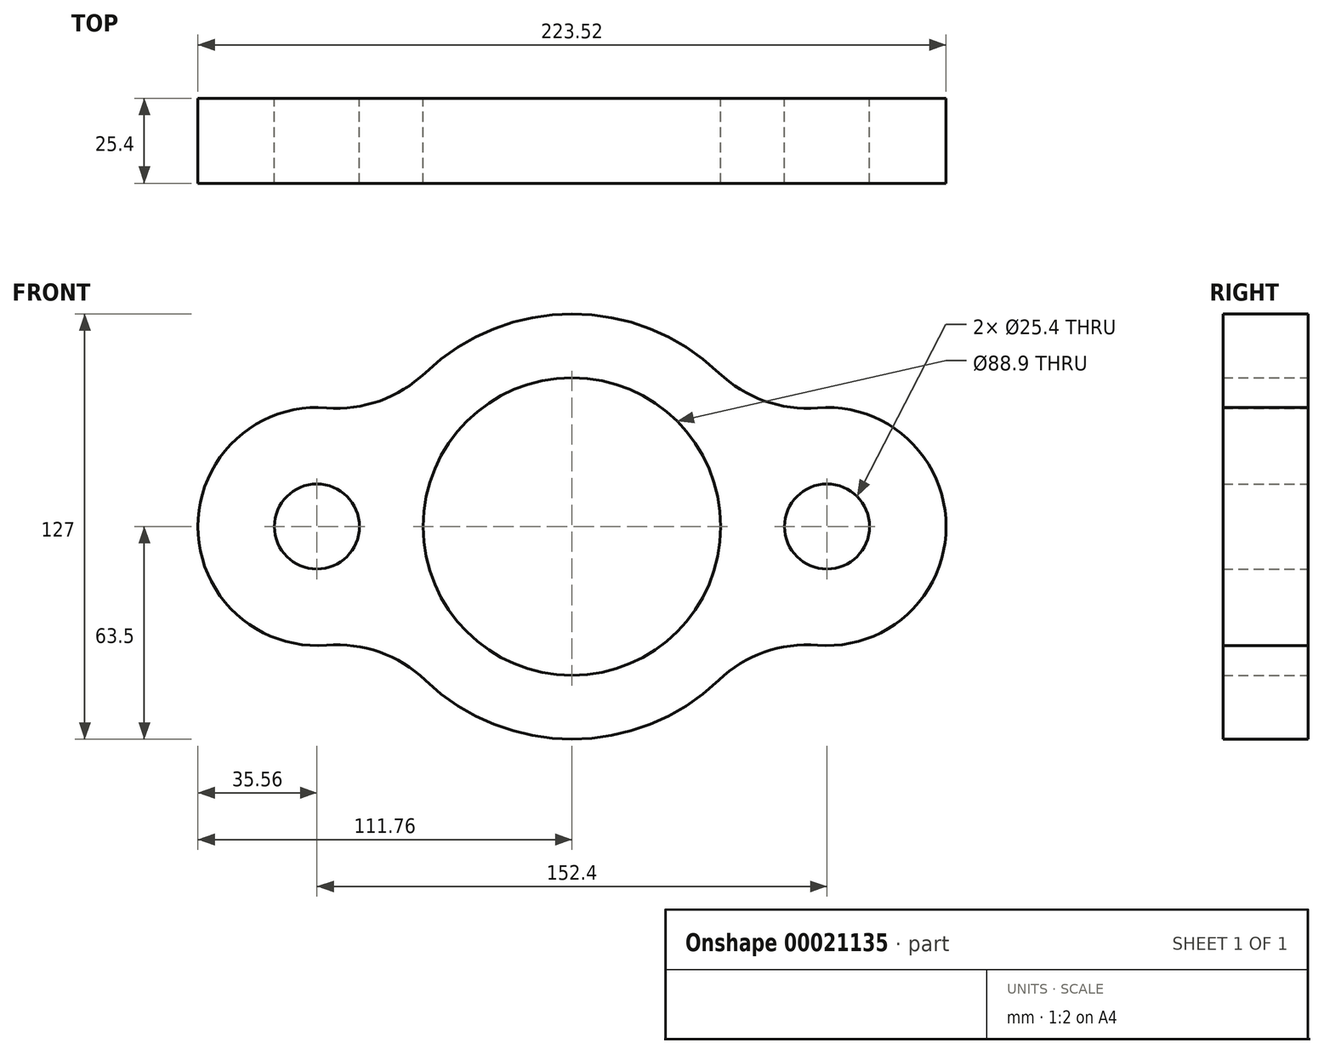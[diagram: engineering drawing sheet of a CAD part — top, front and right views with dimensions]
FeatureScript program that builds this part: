
annotation { "Feature Type Name" : "Feature", "Feature Type Description" : "" }
export const myFeature = defineFeature(function(context is Context, id is Id, definition is map)
    precondition{}
    {
        {
            var Q0;
            Q0=qCreatedBy(makeId("Front.planeOp"),FACE);
            var sketch = newSketch(context, id + "F0", { "sketchPlane" : qUnion([Q0])});
            skCircle(sketch, "E0", {"center": v(0, 0) * mm, "radius": 63.5 * mm});
            skCircle(sketch, "E1", {"center": v(-76.2, 0) * mm, "radius": 35.56 * mm});
            skCircle(sketch, "E2", {"center": v(76.2, 0) * mm, "radius": 35.56 * mm});
            skArc(sketch, "E3", {"start": v(-73.32, 35.44) * mm, "mid": v(-57.49, 37.51) * mm, "end": v(-43.9, 45.89) * mm});
            skArc(sketch, "E4", {"start": v(43.9, 45.89) * mm, "mid": v(57.49, 37.51) * mm, "end": v(73.32, 35.44) * mm});
            skArc(sketch, "E5", {"start": v(-43.9, -45.89) * mm, "mid": v(-57.49, -37.51) * mm, "end": v(-73.32, -35.44) * mm});
            skArc(sketch, "E6", {"start": v(73.32, -35.44) * mm, "mid": v(57.49, -37.51) * mm, "end": v(43.9, -45.89) * mm});
            skCircle(sketch, "E7", {"center": v(0, 0) * mm, "radius": 44.45 * mm});
            skCircle(sketch, "E8", {"center": v(-76.2, 0) * mm, "radius": 12.7 * mm});
            skCircle(sketch, "E9", {"center": v(76.2, 0) * mm, "radius": 12.7 * mm});
            skSolve(sketch);
        }
        {
            var Q0;
            Q0 = qSketchRegion(id + "F0", true);
            var Q1;
            {var subQ4=sQuery(id+"F0.wireOp",EDGE,"E0");var subQ7=makeQuery(id+"F0.imprint","INTERSECT",VERTEX,{"derivedFrom":[subQ4,sQuery(id+"F0.wireOp",EDGE,"E8")]});Q1=makeQuery(id+"F0.imprint","IMPRINT",FACE,{"disambiguationData":[TD([[makeQuery(id+"F0.imprint","IMPRINT",EDGE,{"disambiguationData":[TD([[subQ7,1.0]])],"derivedFrom":subQ4}),1.0]])]});}
            var Q2;
            {var subQ4=sQuery(id+"F0.wireOp",EDGE,"E0");var subQ7=makeQuery(id+"F0.imprint","INTERSECT",VERTEX,{"derivedFrom":[subQ4,sQuery(id+"F0.wireOp",EDGE,"E9")]});Q2=makeQuery(id+"F0.imprint","IMPRINT",FACE,{"disambiguationData":[TD([[makeQuery(id+"F0.imprint","IMPRINT",EDGE,{"disambiguationData":[TD([[subQ7,-1.0]])],"derivedFrom":subQ4}),1.0]])]});}
            extrude(context, id + "F1", {"entities" : qUnion([Q0, Q1, Q2]), "depth" : 25.4 * mm});
        }
    });
